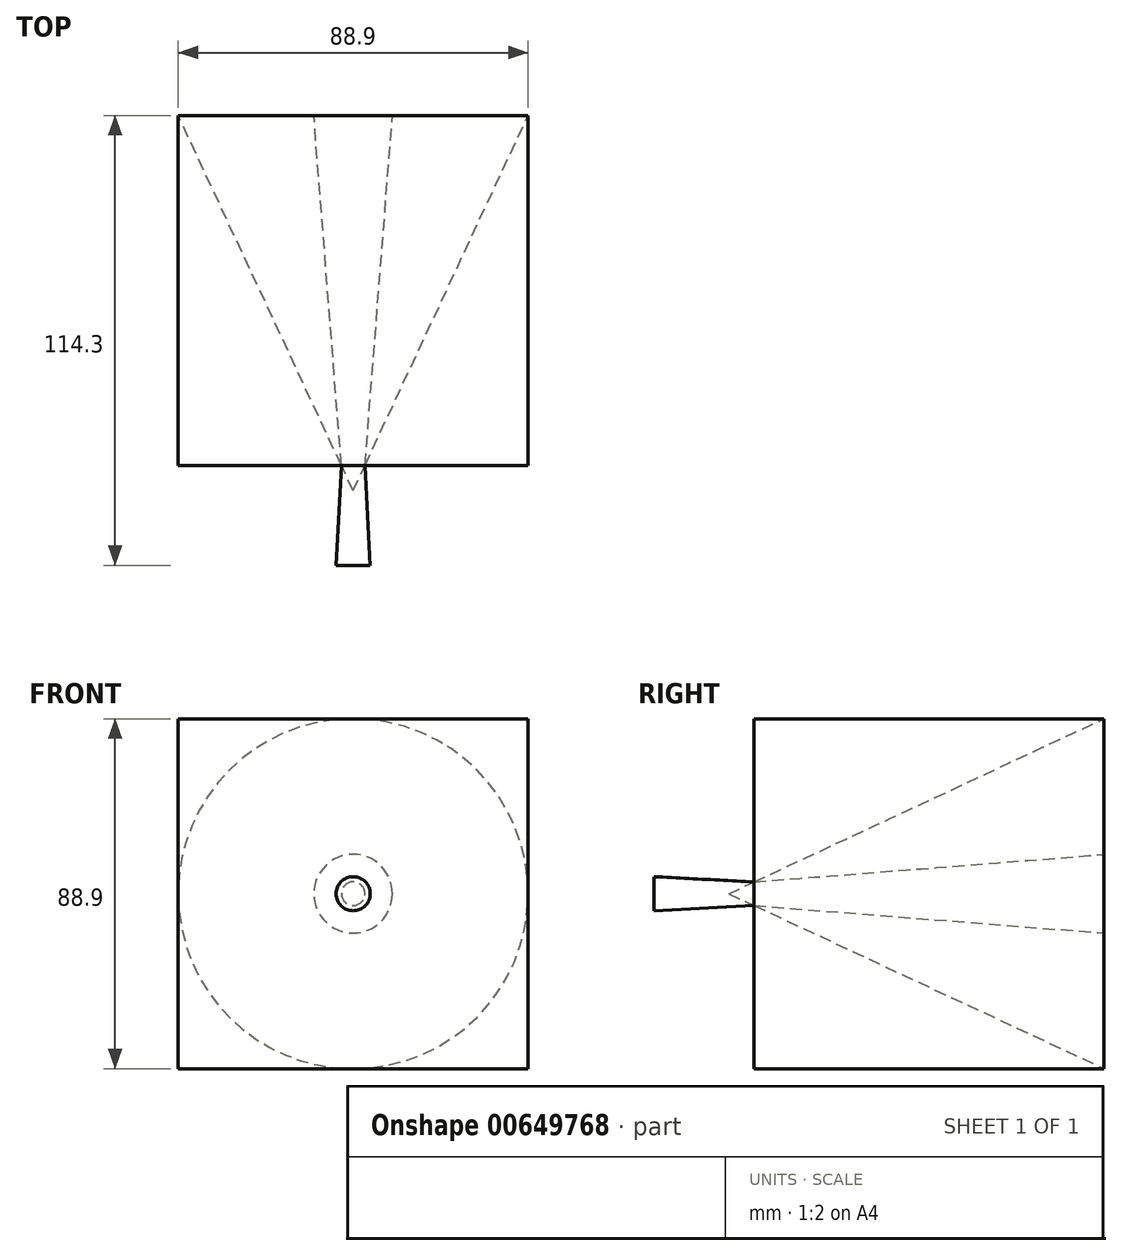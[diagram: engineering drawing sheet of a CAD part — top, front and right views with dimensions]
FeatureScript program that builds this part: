
annotation { "Feature Type Name" : "Feature", "Feature Type Description" : "" }
export const myFeature = defineFeature(function(context is Context, id is Id, definition is map)
    precondition{}
    {
        {
            var Q0;
            Q0=qCreatedBy(makeId("Top.planeOp"),FACE);
            var sketch = newSketch(context, id + "F0", { "sketchPlane" : qUnion([Q0])});
            skLineSegment(sketch, "E0.bottom", {"start": v(-44.45, 44.45) * mm, "end": v(44.45, 44.45) * mm});
            skLineSegment(sketch, "E0.top", {"start": v(-44.45, -44.45) * mm, "end": v(44.45, -44.45) * mm});
            skLineSegment(sketch, "E0.left", {"start": v(-44.45, 44.45) * mm, "end": v(-44.45, -44.45) * mm});
            skLineSegment(sketch, "E0.right", {"start": v(44.45, 44.45) * mm, "end": v(44.45, -44.45) * mm});
            skLineSegment(sketch, "E1", {"start": v(0, 44.45) * mm, "end": v(0, -44.45) * mm, "construction": true});
            skSolve(sketch);
        }
        {
            var Q0;
            Q0 = qSketchRegion(id + "F0", true);
            extrude(context, id + "F1", {"entities" : qUnion([Q0]), "depth" : 44.45 * mm, "offsetDistance" : 25.4 * mm, "hasSecondDirection" : true, "secondDirectionOppositeDirection" : true, "secondDirectionDepth" : 44.45 * mm});
        }
        {
            var Q0;
            Q0=makeQuery(id+"F1.opExtrude","SWEPT_FACE",FACE,{"disambiguationData":[OSD([sQuery(id+"F0.wireOp",EDGE,"E0.bottom")])]});
            var sketch = newSketch(context, id + "F2", { "sketchPlane" : qUnion([Q0])});
            skCircle(sketch, "E2", {"center": v(0, 0) * mm, "radius": 44.45 * mm});
            skSolve(sketch);
        }
        {
            var Q0;
            Q0 = qSketchRegion(id + "F2", true);
            extrude(context, id + "F3", {"entities" : qUnion([Q0]), "operationType" : NewBodyOperationType.REMOVE, "endBound" : BoundingType.THROUGH_ALL, "oppositeDirection" : true, "depth" : 25.4 * mm, "offsetDistance" : 25.4 * mm, "hasDraft" : true, "draftAngle" : 25 * degree, "draftPullDirection" : true});
        }
        {
            var Q0;
            Q0=makeQuery(id+"F1.opExtrude","SWEPT_FACE",FACE,{"disambiguationData":[OSD([sQuery(id+"F0.wireOp",EDGE,"E0.top")])]});
            var sketch = newSketch(context, id + "F4", { "sketchPlane" : qUnion([Q0])});
            skCircle(sketch, "E3", {"center": v(0, 0) * mm, "radius": 3 * mm});
            skSolve(sketch);
        }
        {
            var Q0;
            Q0 = qSketchRegion(id + "F4", true);
            var Q1;
            {var subQ0=sQuery(id+"F0.wireOp",EDGE,"E0.bottom");var subQ1=makeQuery(id+"F1.opExtrude","SWEPT_FACE",FACE,{"disambiguationData":[OSD([subQ0])]});var subQ2=sQuery(id+"F0.wireOp",EDGE,"E0.right");Q1=makeQuery(id+"F3.boolean.opBoolean","SPLIT",FACE,{"disambiguationData":[TD([subQ1,makeQuery(id+"F1.opExtrude","CAP_FACE",FACE,{"disambiguationData":[OSD([subQ0,sQuery(id+"F0.wireOp",EDGE,"E0.top"),sQuery(id+"F0.wireOp",EDGE,"E0.left"),subQ2])],"isStart":false}),makeQuery(id+"F1.opExtrude","SWEPT_FACE",FACE,{"disambiguationData":[OSD([subQ2])]}),makeQuery(id+"F3.opExtrude","SWEPT_FACE",FACE,{"disambiguationData":[OSD([sQuery(id+"F2.wireOp",EDGE,"E2")])]})])],"derivedFrom":subQ1});}
            extrude(context, id + "F5", {"entities" : qUnion([Q0]), "endBound" : BoundingType.UP_TO_SURFACE, "oppositeDirection" : true, "depth" : 101.6 * mm, "endBoundEntityFace" : qUnion([Q1]), "offsetDistance" : 25.4 * mm, "hasDraft" : true, "draftAngle" : 4.5 * degree, "hasSecondDirection" : true, "secondDirectionOppositeDirection" : false, "secondDirectionDepth" : 25.4 * mm, "hasSecondDirectionDraft" : true, "secondDirectionDraftAngle" : 3 * degree});
        }
    });
